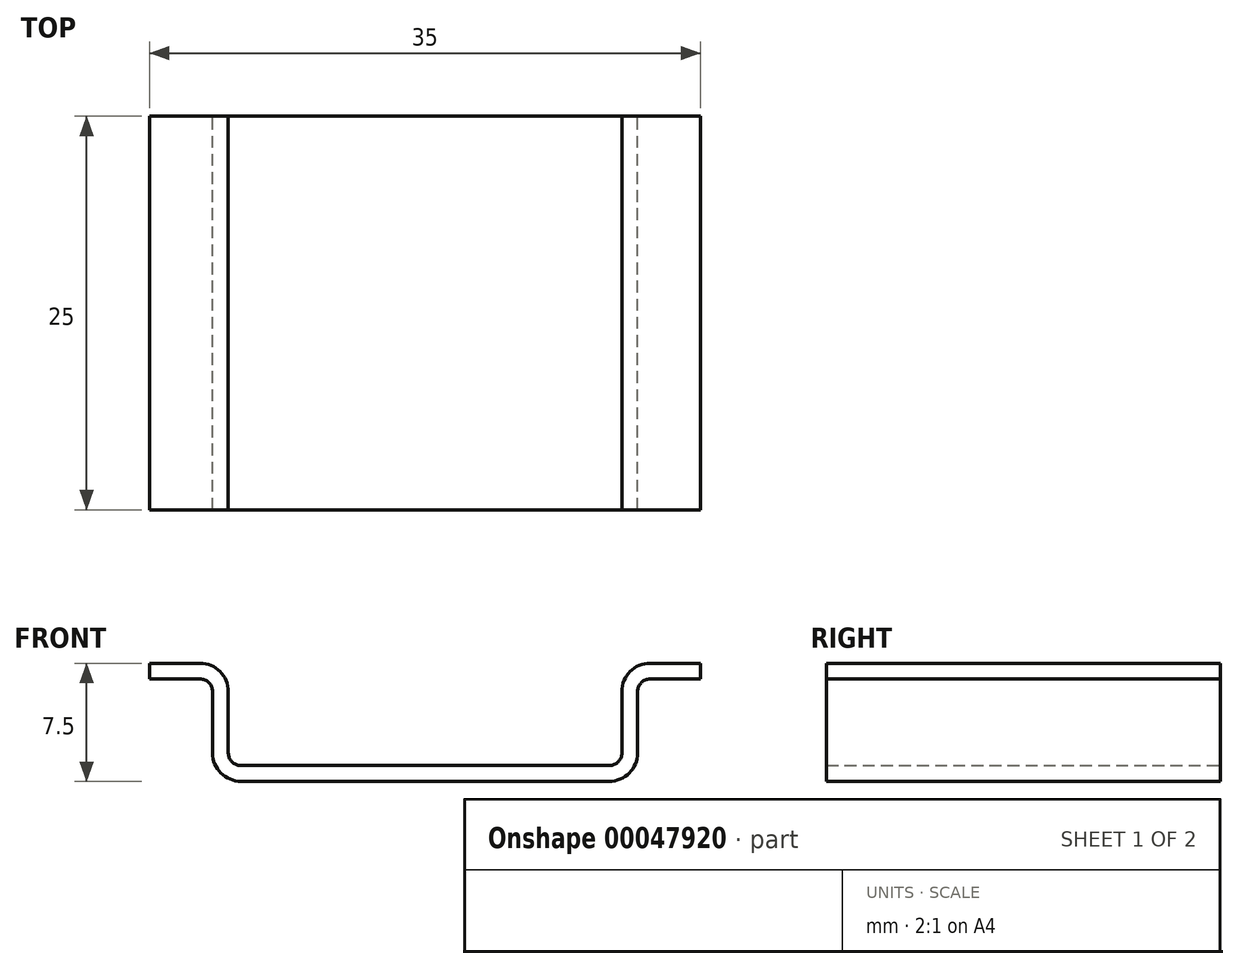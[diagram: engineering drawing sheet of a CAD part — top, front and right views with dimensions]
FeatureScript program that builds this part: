
annotation { "Feature Type Name" : "Feature", "Feature Type Description" : "" }
export const myFeature = defineFeature(function(context is Context, id is Id, definition is map)
    precondition{}
    {
        {
            var Q0;
            Q0=qCreatedBy(makeId("Front.planeOp"),FACE);
            var sketch = newSketch(context, id + "F0", { "sketchPlane" : qUnion([Q0])});
            skLineSegment(sketch, "E0", {"start": v(0, 0) * mm, "end": v(-11.7, 0) * mm});
            skLineSegment(sketch, "E1", {"start": v(-13.5, 1.8) * mm, "end": v(-13.5, 5.7) * mm});
            skLineSegment(sketch, "E2", {"start": v(-14.3, 6.5) * mm, "end": v(-17.5, 6.5) * mm});
            skLineSegment(sketch, "E3.0", {"start": v(-14.3, 7.5) * mm, "end": v(-17.5, 7.5) * mm});
            skLineSegment(sketch, "E3.1", {"start": v(-12.5, 1.8) * mm, "end": v(-12.5, 5.7) * mm});
            skLineSegment(sketch, "E3.2", {"start": v(0, 1) * mm, "end": v(-11.7, 1) * mm});
            skLineSegment(sketch, "E4", {"start": v(-17.5, 7.5) * mm, "end": v(-17.5, 6.5) * mm});
            skPoint(sketch, "E5.visualSharp", {"position": v(-13.5, 6.5) * mm});
            skArc(sketch, "E5.filletArc", {"start": v(-13.5, 5.7) * mm, "mid": v(-13.73, 6.27) * mm, "end": v(-14.3, 6.5) * mm});
            skPoint(sketch, "E6.visualSharp", {"position": v(-12.5, 1) * mm});
            skArc(sketch, "E6.filletArc", {"start": v(-12.5, 1.8) * mm, "mid": v(-12.27, 1.23) * mm, "end": v(-11.7, 1) * mm});
            skArc(sketch, "E7.0", {"start": v(-12.5, 5.7) * mm, "mid": v(-13.03, 6.97) * mm, "end": v(-14.3, 7.5) * mm});
            skArc(sketch, "E8.0", {"start": v(-13.5, 1.8) * mm, "mid": v(-12.97, 0.53) * mm, "end": v(-11.7, 0) * mm});
            skLineSegment(sketch, "E9", {"start": v(0, 3.23) * mm, "end": v(0, -3.23) * mm, "construction": true});
            skLineSegment(sketch, "E10.MirrorCS", {"start": v(0, 1) * mm, "end": v(11.7, 1) * mm});
            skLineSegment(sketch, "E11.MirrorCS", {"start": v(0, 0) * mm, "end": v(11.7, 0) * mm});
            skLineSegment(sketch, "E12.MirrorCS", {"start": v(17.5, 7.5) * mm, "end": v(17.5, 6.5) * mm});
            skArc(sketch, "E13.MirrorCS", {"start": v(12.5, 1.8) * mm, "mid": v(12.27, 1.23) * mm, "end": v(11.7, 1) * mm});
            skArc(sketch, "E14.MirrorCS", {"start": v(13.5, 5.7) * mm, "mid": v(13.73, 6.27) * mm, "end": v(14.3, 6.5) * mm});
            skPoint(sketch, "E15.MirrorP", {"position": v(12.5, 1) * mm});
            skLineSegment(sketch, "E16.MirrorCS", {"start": v(14.3, 6.5) * mm, "end": v(17.5, 6.5) * mm});
            skLineSegment(sketch, "E17.MirrorCS", {"start": v(13.5, 1.8) * mm, "end": v(13.5, 5.7) * mm});
            skLineSegment(sketch, "E18.MirrorCS", {"start": v(14.3, 7.5) * mm, "end": v(17.5, 7.5) * mm});
            skLineSegment(sketch, "E19.MirrorCS", {"start": v(12.5, 1.8) * mm, "end": v(12.5, 5.7) * mm});
            skArc(sketch, "E20.MirrorCS", {"start": v(12.5, 5.7) * mm, "mid": v(13.03, 6.97) * mm, "end": v(14.3, 7.5) * mm});
            skArc(sketch, "E21.MirrorCS", {"start": v(13.5, 1.8) * mm, "mid": v(12.97, 0.53) * mm, "end": v(11.7, 0) * mm});
            skPoint(sketch, "E22.MirrorP", {"position": v(13.5, 6.5) * mm});
            skSolve(sketch);
        }
        {
            var Q0;
            Q0 = qSketchRegion(id + "F0", true);
            extrude(context, id + "F1", {"entities" : qUnion([Q0]), "depth" : 25 * mm});
        }
    });
